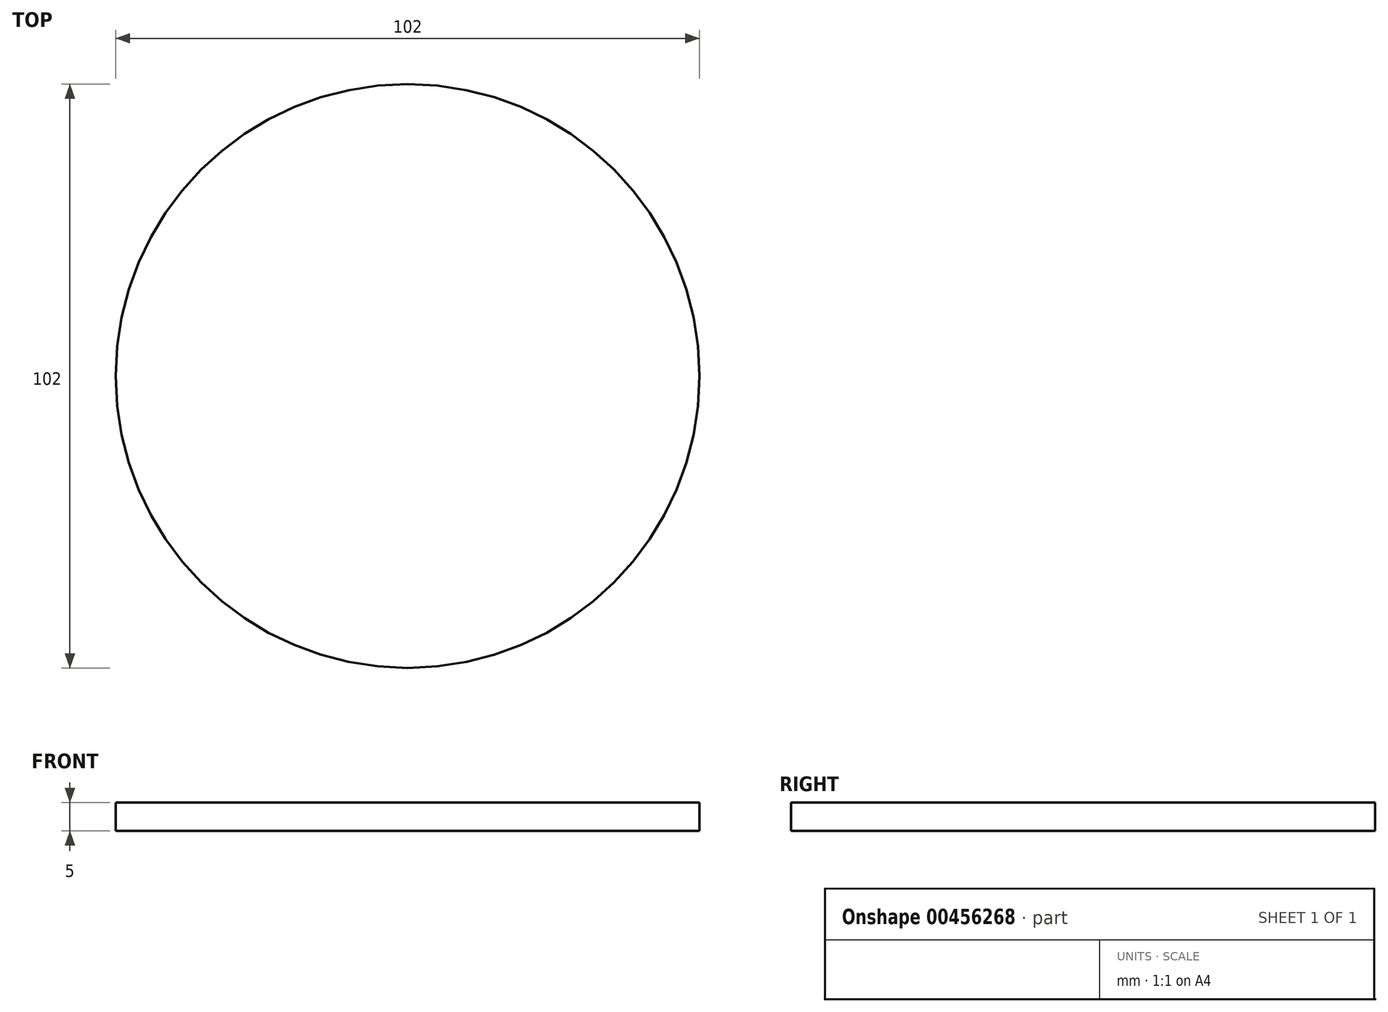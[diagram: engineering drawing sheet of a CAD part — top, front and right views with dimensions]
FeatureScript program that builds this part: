
annotation { "Feature Type Name" : "Feature", "Feature Type Description" : "" }
export const myFeature = defineFeature(function(context is Context, id is Id, definition is map)
    precondition{}
    {
        {
            var Q0;
            Q0=qCreatedBy(makeId("Top.planeOp"),FACE);
            var sketch = newSketch(context, id + "F0", { "sketchPlane" : qUnion([Q0])});
            skCircle(sketch, "E0", {"center": v(0, 0) * mm, "radius": 51 * mm});
            skSolve(sketch);
        }
        {
            var Q0;
            Q0=makeQuery(id+"F0.imprint","IMPRINT",FACE,{"disambiguationData":[TD([[makeQuery(id+"F0.imprint","IMPRINT",EDGE,{"derivedFrom":sQuery(id+"F0.wireOp",EDGE,"E0")}),1.0]])]});
            extrude(context, id + "F1", {"entities" : qUnion([Q0]), "depth" : 5 * mm, "offsetDistance" : 25 * mm});
        }
    });
